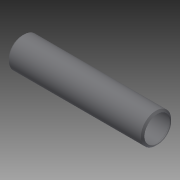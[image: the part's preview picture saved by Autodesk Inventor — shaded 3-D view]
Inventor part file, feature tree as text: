
AUTODESK INVENTOR PART (.ipt)
format: ipt  version: 2014 (Build 180170000, 170)  size: 122,880 bytes
history: native  units: in
note: dims shown in document units (in); Inventor stores cm internally (conversion verified against a paired STEP export)
features: other x56, revolve x1, sketch x1
ambient origin geometry x8: Origin, YZ Plane, XZ Plane, XY Plane, X Axis, Y Axis, Z Axis, Center Point
bodies: Solid1 (feature_tree)
feature tree (58):
  revolve  "Revolution1"  [1 undecoded]
  other  "o1_XY"
  other  "o1_YZ"
  other  "o1_ZX"
  other  "o1_X"
  other  "o1_Y"
  other  "o1_Z"
  other  "o1_Center"
  other  "o2_XY"
  other  "o2_YZ"
  other  "o2_ZX"
  other  "o2_X"
  other  "o2_Y"
  other  "o2_Z"
  other  "o2_Center"
  other  "t1_XY"
  other  "t1_YZ"
  other  "t1_ZX"
  other  "t1_X"
  other  "t1_Y"
  other  "t1_Z"
  other  "t1_Center"
  other  "t2_XY"
  other  "t2_YZ"
  other  "t2_ZX"
  other  "t2_X"
  other  "t2_Y"
  other  "t2_Z"
  other  "t2_Center"
  other  "t3_XY"
  other  "t3_YZ"
  other  "t3_ZX"
  other  "t3_X"
  other  "t3_Y"
  other  "t3_Z"
  other  "t3_Center"
  other  "t4_XY"
  other  "t4_YZ"
  other  "t4_ZX"
  other  "t4_X"
  other  "t4_Y"
  other  "t4_Z"
  other  "t4_Center"
  other  "tube1_XY"
  other  "tube1_YZ"
  other  "tube1_ZX"
  other  "tube1_X"
  other  "tube1_Y"
  other  "tube1_Z"
  other  "tube1_Center"
  other  "tube2_XY"
  other  "tube2_YZ"
  other  "tube2_ZX"
  other  "tube2_X"
  other  "tube2_Y"
  other  "tube2_Z"
  other  "tube2_Center"
  sketch  "Sketch_5"  dims[d0=360.0deg]
note: 1 required parameter value undecoded (feature->parameter linkage not recoverable at this tier; creation-order binding heuristic only, values carry confidence <= 0.55)
